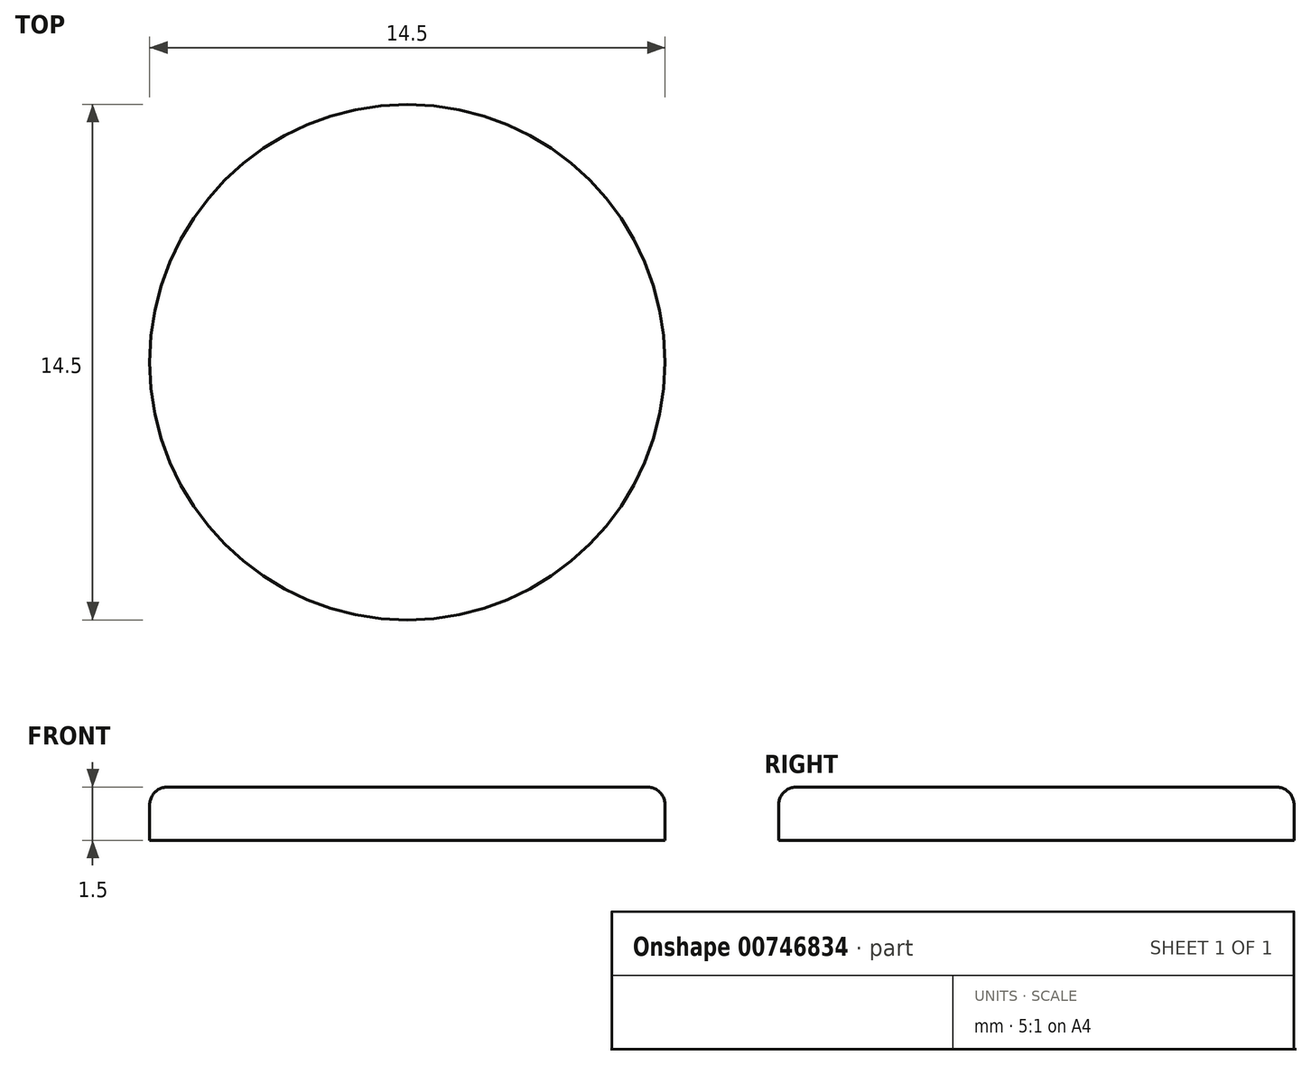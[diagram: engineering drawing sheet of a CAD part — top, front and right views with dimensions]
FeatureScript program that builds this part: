
annotation { "Feature Type Name" : "Feature", "Feature Type Description" : "" }
export const myFeature = defineFeature(function(context is Context, id is Id, definition is map)
    precondition{}
    {
        {
            var Q0;
            Q0=qCreatedBy(makeId("Top.planeOp"),FACE);
            var sketch = newSketch(context, id + "F0", { "sketchPlane" : qUnion([Q0])});
            skCircle(sketch, "E0", {"center": v(0, 0) * mm, "radius": 7.25 * mm});
            skSolve(sketch);
        }
        {
            var Q0;
            Q0=makeQuery(id+"F0.imprint","IMPRINT",FACE,{"disambiguationData":[TD([[makeQuery(id+"F0.imprint","IMPRINT",EDGE,{"derivedFrom":sQuery(id+"F0.wireOp",EDGE,"E0")}),1.0]])]});
            extrude(context, id + "F1", {"entities" : qUnion([Q0]), "depth" : 1.5 * mm, "offsetDistance" : 25 * mm});
        }
        {
            var Q0;
            Q0=makeQuery(id+"F1.opExtrude","CAP_FACE",FACE,{"disambiguationData":[OSD([sQuery(id+"F0.wireOp",EDGE,"E0")])],"isStart":false});
            fillet(context, id + "F2", {"entities" : qUnion([Q0]), "radius" : 0.5 * mm, "tangentPropagation" : true, "allowEdgeOverflow" : false});
        }
    });
